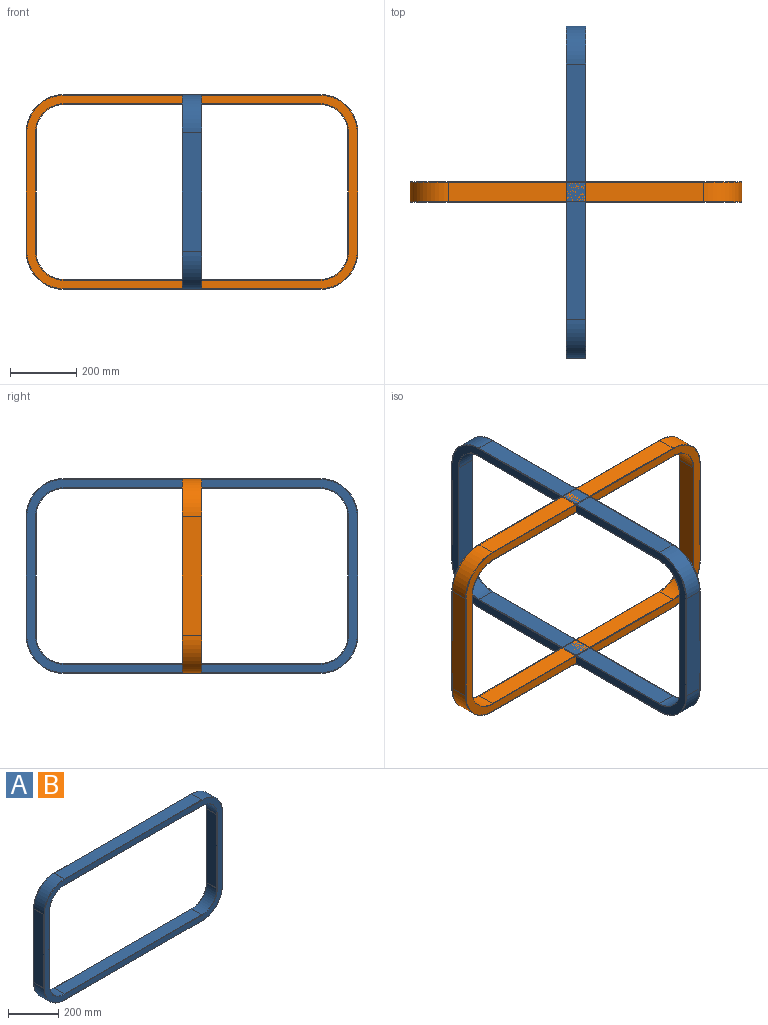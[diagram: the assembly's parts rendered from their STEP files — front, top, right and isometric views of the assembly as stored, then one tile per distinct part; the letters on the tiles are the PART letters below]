
ASSEMBLY  parts=2 mates=1
PART A: 68 faces, bbox 1019x60x607 mm
  f0: cylinder r=115mm len=115mm, axis (0,-1,0), area 10405mm2, adj f1,f5,f6,f42
  f1: torus R=113.8mm, axis (0,-1,0), area 339.2mm2, adj f0,f7,f43,f44
  f2: torus R=86.2mm, axis (0,-1,0), area 253mm2, adj f3,f8,f44,f45
  f3: cylinder r=85mm len=85mm, axis (0,-1,0), area 7690.6mm2, adj f2,f4,f9,f46
  f4: torus R=86.2mm, axis (0,-1,0), area 253mm2, adj f3,f10,f47,f48
  f5: torus R=113.8mm, axis (0,-1,0), area 339.2mm2, adj f0,f11,f48,f49
  f6: plane 358x57.6mm, normal (-1,0,0), area 20620.8mm2, adj f0,f7,f11,f12
  f7: cylinder r=1.2mm len=358mm, axis (0,0,-1), area 674.8mm2, adj f1,f6,f13,f44
  f8: cylinder r=1.2mm len=358mm, axis (0,0,-1), area 674.8mm2, adj f2,f9,f14,f44
  f9: plane 358x57.6mm, normal (1,0,0), area 20620.8mm2, adj f3,f8,f10,f15
  f10: cylinder r=1.2mm len=358mm, axis (0,0,-1), area 674.8mm2, adj f4,f9,f16,f48
  f11: cylinder r=1.2mm len=358mm, axis (0,0,-1), area 674.8mm2, adj f5,f6,f17,f48
  f12: cylinder r=115mm len=115mm, axis (0,-1,0), area 10405mm2, adj f6,f13,f17,f18
  f13: torus R=113.8mm, axis (0,-1,0), area 339.2mm2, adj f7,f12,f19,f44
  f14: torus R=86.2mm, axis (0,-1,0), area 253mm2, adj f8,f15,f20,f44
  f15: cylinder r=85mm len=85mm, axis (0,-1,0), area 7690.6mm2, adj f9,f14,f16,f21
  f16: torus R=86.2mm, axis (0,-1,0), area 253mm2, adj f10,f15,f22,f48
  f17: torus R=113.8mm, axis (0,-1,0), area 339.2mm2, adj f11,f12,f23,f48
  f18: plane 770x57.6mm, normal (0,0,1), area 44352mm2, adj f12,f19,f23,f24
  f19: cylinder r=1.2mm len=770mm, axis (-1,0,0), area 1451.4mm2, adj f13,f18,f25,f44
  f20: cylinder r=1.2mm len=770mm, axis (-1,0,0), area 1451.4mm2, adj f14,f21,f26,f44
  f21: plane 770x57.6mm, normal (0,0,-1), area 44352mm2, adj f15,f20,f22,f27
  f22: cylinder r=1.2mm len=770mm, axis (-1,0,0), area 1451.4mm2, adj f16,f21,f28,f48
  f23: cylinder r=1.2mm len=770mm, axis (-1,0,0), area 1451.4mm2, adj f17,f18,f29,f48
  f24: cylinder r=115mm len=115mm, axis (0,-1,0), area 10405mm2, adj f18,f25,f29,f30
  f25: torus R=113.8mm, axis (0,-1,0), area 339.2mm2, adj f19,f24,f31,f44
  f26: torus R=86.2mm, axis (0,-1,0), area 253mm2, adj f20,f27,f32,f44
  f27: cylinder r=85mm len=85mm, axis (0,-1,0), area 7690.6mm2, adj f21,f26,f28,f33
  f28: torus R=86.2mm, axis (0,-1,0), area 253mm2, adj f22,f27,f34,f48
  f29: torus R=113.8mm, axis (0,-1,0), area 339.2mm2, adj f23,f24,f35,f48
  f30: plane 358x57.6mm, normal (1,0,0), area 20620.8mm2, adj f24,f31,f35,f36
  f31: cylinder r=1.2mm len=358mm, axis (0,0,1), area 674.8mm2, adj f25,f30,f37,f44
  f32: cylinder r=1.2mm len=358mm, axis (0,0,1), area 674.8mm2, adj f26,f33,f38,f44
  f33: plane 358x57.6mm, normal (-1,0,0), area 20620.8mm2, adj f27,f32,f34,f39
  f34: cylinder r=1.2mm len=358mm, axis (0,0,1), area 674.8mm2, adj f28,f33,f40,f48
  f35: cylinder r=1.2mm len=358mm, axis (0,0,1), area 674.8mm2, adj f29,f30,f41,f48
  f36: cylinder r=115mm len=115mm, axis (0,-1,0), area 10405mm2, adj f30,f37,f41,f42
  f37: torus R=113.8mm, axis (0,-1,0), area 339.2mm2, adj f31,f36,f43,f44
  f38: torus R=86.2mm, axis (0,-1,0), area 253mm2, adj f32,f39,f44,f45
  f39: cylinder r=85mm len=85mm, axis (0,-1,0), area 7690.6mm2, adj f33,f38,f40,f46
  f40: torus R=86.2mm, axis (0,-1,0), area 253mm2, adj f34,f39,f47,f48
  f41: torus R=113.8mm, axis (0,-1,0), area 339.2mm2, adj f35,f36,f48,f49
  f42: plane 770x57.6mm, normal (0,0,-1), area 44352mm2, adj f0,f36,f43,f49
  f43: cylinder r=1.2mm len=770mm, axis (1,0,0), area 1451.4mm2, adj f1,f37,f42,f44
  f44: plane 997.6x585.6mm, normal (0,-1,0), area 79607.2mm2, adj f1,f2,f7,f8,f13,f14,f19,f20
  f45: cylinder r=1.2mm len=770mm, axis (1,0,0), area 1451.4mm2, adj f2,f38,f44,f46
  f46: plane 770x57.6mm, normal (0,0,1), area 44352mm2, adj f3,f39,f45,f47
  f47: cylinder r=1.2mm len=770mm, axis (1,0,0), area 1451.4mm2, adj f4,f40,f46,f48
  f48: plane 997.6x585.6mm, normal (0,1,0), area 79607.2mm2, adj f4,f5,f10,f11,f16,f17,f22,f23
  f49: cylinder r=1.2mm len=770mm, axis (1,0,0), area 1451.4mm2, adj f5,f41,f42,f48
  f50: cylinder r=87mm len=87mm, axis (0,-1,0), area 7652.9mm2, adj f51,f53,f54,f66
  f51: plane 996x584mm, normal (0,1,0), area 74992.3mm2, adj f50,f52,f54,f55,f56,f57,f58,f59
  f52: cylinder r=113mm len=113mm, axis (0,-1,0), area 9940mm2, adj f51,f53,f55,f67
  f53: plane 996x584mm, normal (0,-1,0), area 74992.3mm2, adj f50,f52,f54,f55,f56,f57,f58,f59
  f54: plane 358x56mm, normal (-1,0,0), area 20048mm2, adj f50,f51,f53,f56
  f55: plane 358x56mm, normal (1,0,0), area 20048mm2, adj f51,f52,f53,f57
  f56: cylinder r=87mm len=87mm, axis (0,-1,0), area 7652.9mm2, adj f51,f53,f54,f58
  f57: cylinder r=113mm len=113mm, axis (0,-1,0), area 9940mm2, adj f51,f53,f55,f59
  f58: plane 770x56mm, normal (0,0,1), area 43120mm2, adj f51,f53,f56,f60
  f59: plane 770x56mm, normal (0,0,-1), area 43120mm2, adj f51,f53,f57,f61
  f60: cylinder r=87mm len=87mm, axis (0,-1,0), area 7652.9mm2, adj f51,f53,f58,f62
  f61: cylinder r=113mm len=113mm, axis (0,-1,0), area 9940mm2, adj f51,f53,f59,f63
  f62: plane 358x56mm, normal (1,0,0), area 20048mm2, adj f51,f53,f60,f64
  f63: plane 358x56mm, normal (-1,0,0), area 20048mm2, adj f51,f53,f61,f65
  f64: cylinder r=87mm len=87mm, axis (0,-1,0), area 7652.9mm2, adj f51,f53,f62,f66
  f65: cylinder r=113mm len=113mm, axis (0,-1,0), area 9940mm2, adj f51,f53,f63,f67
  f66: plane 770x56mm, normal (0,0,-1), area 43120mm2, adj f50,f51,f53,f64
  f67: plane 770x56mm, normal (0,0,1), area 43120mm2, adj f51,f52,f53,f65
PART B: same geometry as A
PLACE A rot(axis=(0,0,1),90deg) t=(-134.84,132.53,-38.44)mm
PLACE B t=(-134.84,132.53,-38.44)mm
MATE fastened A.f18 <-> B.f18  axis (0,0,1) through (-134.84,132.53,534.56)mm
